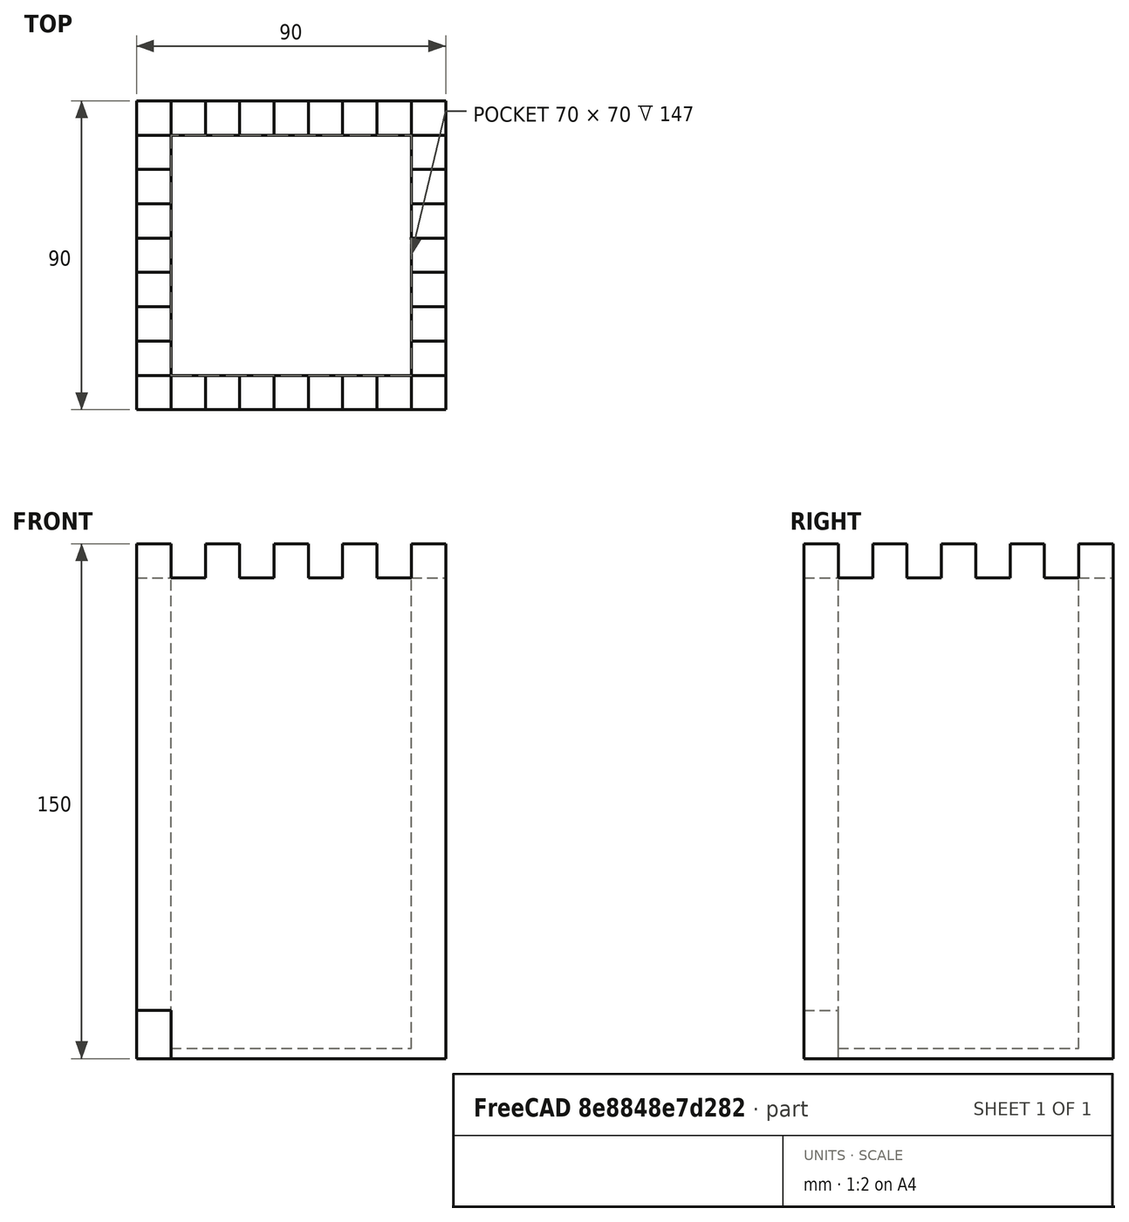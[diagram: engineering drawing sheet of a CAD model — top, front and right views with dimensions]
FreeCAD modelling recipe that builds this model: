
FCSTD DOCUMENT  (FreeCAD 0.21R33694 (Git))
Label: OJT1_T10R02_castell
License: All rights reserved
LicenseURL: http://en.wikipedia.org/wiki/All_rights_reserved
objects: Part::Box×4, Part::Cut×3, Part::FeaturePython×1
note: 7 computed .brp shape members not serialized (recipe doc carries the construction recipe); baked Part::Feature solids carry a one-line shape summary decoded from their .brp

FEATURE [Part::Box] Box  label="Cube"
  AttacherType = Attacher::AttachEngine3D
  Height = 150
  Length = 90
  Width = 90
FEATURE [Part::Box] Box001  label="Cube001"
  AttacherType = Attacher::AttachEngine3D
  Height = 14
  Length = 10
  Width = 10
FEATURE [Part::FeaturePython] Array  # Draft array (typed FeaturePython)
  AlwaysSyncPlacement = false
  Angle = 360
  ArrayType = 0
  Axis = (0,0,1)
  Base = -> Box001
  Center = (0,0,0)
  Count = 25
  ExpandArray = false
  Fuse = false
  IntervalAxis = (0,0,0)
  IntervalX = (20,0,0)
  IntervalY = (0,20,0)
  IntervalZ = (0,0,100)
  NumberCircles = 3
  NumberPolar = 5
  NumberX = 5
  NumberY = 5
  NumberZ = 1
  PlacementList = 25 placements: [(0,0,0),(0,20,0),(0,40,0),(0,60,0),(0,80,0),(20,0,0),(20,20,0),(20,40,0),(20,60,0),(20,80,0),(40,0,0),(40,20,0),(40,40,0),(40,60,0),(40,80,0),(60,0,0),(60,20,0),(60,40,0),(60,60,0),(60,80,0),(80,0,0),(80,20,0),(80,40,0),(80,60,0),(80,80,0)]
  RadialDistance = 50
  ScaleList = (25) [(1,1,1),(1,1,1),(1,1,1),(1,1,1),(1,1,1),(1,1,1),(1,1,1),(1,1,1),(1,1,1),(1,1,1),(1,1,1),(1,1,1),(1,1,1),(1,1,1),(1,1,1),(1,1,1),(1,1,1),(1,1,1),+7 more]
  Symmetry = 1
  TangentialDistance = 25
FEATURE [Part::Box] Box002  label="Cube002"
  AttacherType = Attacher::AttachEngine3D
  Height = 10
  Length = 110
  Placement = pos=(-10,-9,0) rot=(0,0,1;0rad)
  Width = 110
FEATURE [Part::Cut] Cut
  Base = -> Box002
  Placement = pos=(0,0,140) rot=(0,0,1;0rad)
  Refine = true
  Tool = -> Array
FEATURE [Part::Cut] Cut001
  Base = -> Box
  Refine = true
  Tool = -> Cut
FEATURE [Part::Box] Box003  label="Cube003"
  AttacherType = Attacher::AttachEngine3D
  Height = 150
  Length = 70
  Placement = pos=(10,10,3) rot=(0,0,1;0rad)
  Width = 70
FEATURE [Part::Cut] Cut002
  Base = -> Cut001
  Refine = true
  Tool = -> Box003
